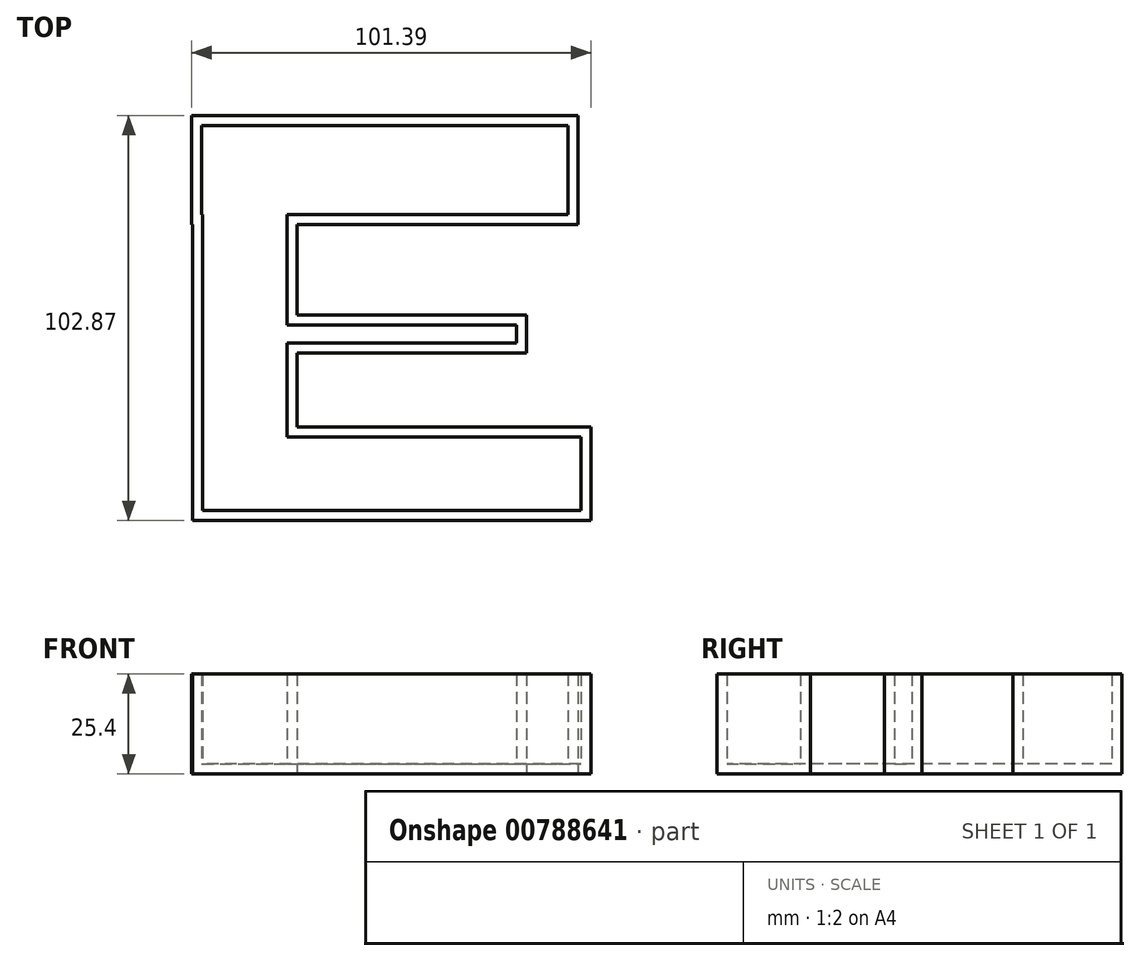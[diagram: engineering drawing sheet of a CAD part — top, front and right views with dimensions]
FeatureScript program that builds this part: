
annotation { "Feature Type Name" : "Feature", "Feature Type Description" : "" }
export const myFeature = defineFeature(function(context is Context, id is Id, definition is map)
    precondition{}
    {
        {
            var Q0;
            Q0=qCreatedBy(makeId("Top.planeOp"),FACE);
            var sketch = newSketch(context, id + "F0", { "sketchPlane" : qUnion([Q0])});
            skLineSegment(sketch, "E0.bottom", {"start": v(-37.33, 55.4) * mm, "end": v(60.74, 55.4) * mm});
            skLineSegment(sketch, "E0.top", {"start": v(-37.33, 27.75) * mm, "end": v(60.74, 27.75) * mm});
            skLineSegment(sketch, "E0.left", {"start": v(-37.33, 55.4) * mm, "end": v(-37.33, 27.75) * mm});
            skLineSegment(sketch, "E0.right", {"start": v(60.74, 55.4) * mm, "end": v(60.74, 27.75) * mm});
            skLineSegment(sketch, "E1.bottom", {"start": v(-10.6, 27.75) * mm, "end": v(-37.15, 27.75) * mm});
            skLineSegment(sketch, "E1.top", {"start": v(-10.6, -47.47) * mm, "end": v(-37.15, -47.47) * mm});
            skLineSegment(sketch, "E1.left", {"start": v(-10.6, 27.75) * mm, "end": v(-10.6, -47.47) * mm});
            skLineSegment(sketch, "E1.right", {"start": v(-37.15, 27.75) * mm, "end": v(-37.15, -47.47) * mm});
            skLineSegment(sketch, "E2.bottom", {"start": v(-10.6, -47.47) * mm, "end": v(64.06, -47.47) * mm});
            skLineSegment(sketch, "E2.top", {"start": v(-10.6, -23.69) * mm, "end": v(64.06, -23.69) * mm});
            skLineSegment(sketch, "E2.left", {"start": v(-10.6, -47.47) * mm, "end": v(-10.6, -23.69) * mm});
            skLineSegment(sketch, "E2.right", {"start": v(64.06, -47.47) * mm, "end": v(64.06, -23.69) * mm});
            skLineSegment(sketch, "E3.bottom", {"start": v(-10.6, -4.89) * mm, "end": v(47.66, -4.89) * mm});
            skLineSegment(sketch, "E3.top", {"start": v(-10.6, 4.7) * mm, "end": v(47.66, 4.7) * mm});
            skLineSegment(sketch, "E3.left", {"start": v(-10.6, -4.89) * mm, "end": v(-10.6, 4.7) * mm});
            skLineSegment(sketch, "E3.right", {"start": v(47.66, -4.89) * mm, "end": v(47.66, 4.7) * mm});
            skSolve(sketch);
        }
        {
            var Q0;
            Q0=makeQuery(id+"F0.imprint","IMPRINT",FACE,{"disambiguationData":[TD([[makeQuery(id+"F0.imprint","IMPRINT",EDGE,{"derivedFrom":sQuery(id+"F0.wireOp",EDGE,"E0.bottom")}),-1.0]])]});
            var Q1;
            {var subQ4=sQuery(id+"F0.wireOp",EDGE,"E1.top");Q1=makeQuery(id+"F0.imprint","IMPRINT",FACE,{"disambiguationData":[TD([[makeQuery(id+"F0.imprint","IMPRINT",EDGE,{"derivedFrom":subQ4}),-1.0]])]});}
            var Q2;
            {var subQ0=sQuery(id+"F0.wireOp",EDGE,"E2.bottom");Q2=makeQuery(id+"F0.imprint","IMPRINT",FACE,{"disambiguationData":[TD([[makeQuery(id+"F0.imprint","IMPRINT",EDGE,{"derivedFrom":subQ0}),1.0]])]});}
            var Q3;
            {var subQ0=sQuery(id+"F0.wireOp",EDGE,"E3.bottom");Q3=makeQuery(id+"F0.imprint","IMPRINT",FACE,{"disambiguationData":[TD([[makeQuery(id+"F0.imprint","IMPRINT",EDGE,{"derivedFrom":subQ0}),1.0]])]});}
            extrude(context, id + "F1", {"entities" : qUnion([Q0, Q1, Q2, Q3]), "depth" : 25.4 * mm, "offsetDistance" : 25.4 * mm});
        }
        {
            var Q0;
            Q0=makeQuery(id+"F1.opExtrude","CAP_FACE",FACE,{"disambiguationData":[OSD([sQuery(id+"F0.wireOp",EDGE,"E0.bottom"),sQuery(id+"F0.wireOp",EDGE,"E0.top"),sQuery(id+"F0.wireOp",EDGE,"E0.left"),sQuery(id+"F0.wireOp",EDGE,"E0.right"),sQuery(id+"F0.wireOp",EDGE,"E1.top"),sQuery(id+"F0.wireOp",EDGE,"E1.left"),sQuery(id+"F0.wireOp",EDGE,"E1.right"),sQuery(id+"F0.wireOp",EDGE,"E2.bottom"),sQuery(id+"F0.wireOp",EDGE,"E2.top"),sQuery(id+"F0.wireOp",EDGE,"E2.right"),sQuery(id+"F0.wireOp",EDGE,"E3.bottom"),sQuery(id+"F0.wireOp",EDGE,"E3.top"),sQuery(id+"F0.wireOp",EDGE,"E3.right")])],"isStart":false});
            shell(context, id + "F2", {"entities" : qUnion([Q0]), "thickness" : 2.54 * mm});
        }
    });
